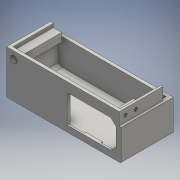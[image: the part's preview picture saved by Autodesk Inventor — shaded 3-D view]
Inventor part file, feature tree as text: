
AUTODESK INVENTOR PART (.ipt)
format: ipt  version: 2016 (Build 200138000, 138)  size: 650,752 bytes
history: native  units: mm
features: extrude x6, sketch x6, projected_geometry x5, other x2, fillet x2
ambient origin geometry x8: Origin, YZ Plane, XZ Plane, XY Plane, X Axis, Y Axis, Z Axis, Center Point
bodies: Solid1 (feature_tree)
feature tree (21):
  other  "psu_cover_20a_i3_steel"
  other  "MeshFeature1"
  extrude  "Extrusion1"  Depth=10.0mm TaperAngle=0.0deg
  extrude  "Extrusion2"  Depth=27.0mm
  extrude  "Extrusion3"  Depth=6.0mm
  extrude  "Extrusion4"  Depth=5.0mm
  extrude  "Extrusion5"  Depth=5.0mm
  fillet  "Fillet1"  Radius=10.0mm
  fillet  "Fillet2"  Radius=10.0mm
  extrude  "Extrusion6"  Depth=10.0mm TaperAngle=0.0deg
  sketch  "Sketch1"  dims[d0=10.0mm d1=0.0mm d2=10.0mm d3=0.0mm]
  projected_geometry  "Projected Loop1"
  sketch  "Sketch2"  dims[d4=47.0mm d5=27.0mm]
  projected_geometry  "Projected Loop2"
  sketch  "Sketch3"  dims[d6=5.0mm d7=6.0mm]
  sketch  "Sketch4"  dims[d8=5.0mm d9=5.0mm]
  projected_geometry  "Projected Loop3"
  sketch  "Sketch5"  dims[d10=5.0mm d11=5.0mm d12=10.0mm d13=0.0mm d14=10.0mm d15=0.0mm]
  projected_geometry  "Projected Loop4"
  sketch  "Sketch6"  dims[d16=14.0mm d17=10.0mm d18=0.0mm d19=3.0mm d20=1.0mm d21=1.5mm d22=15.0mm d23=15.0mm d24=11.0mm d25=11.0mm d26=1.5mm d27=0.0mm]
  projected_geometry  "Projected Loop5"
